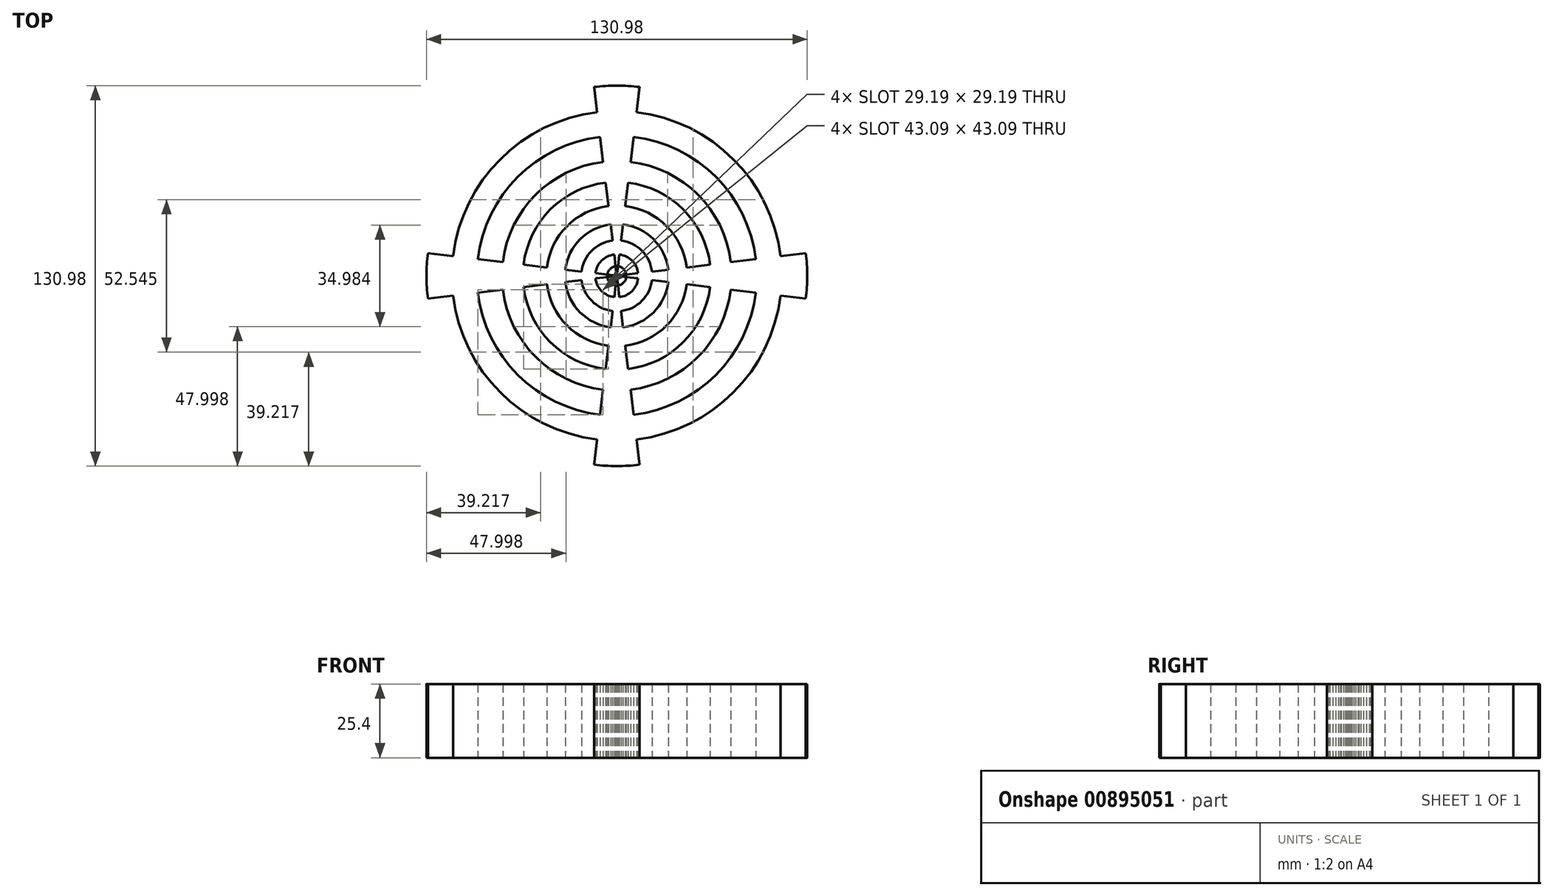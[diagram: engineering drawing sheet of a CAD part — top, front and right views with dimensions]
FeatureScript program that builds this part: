
annotation { "Feature Type Name" : "Feature", "Feature Type Description" : "" }
export const myFeature = defineFeature(function(context is Context, id is Id, definition is map)
    precondition{}
    {
        {
            var Q0;
            Q0=qCreatedBy(makeId("Top.planeOp"),FACE);
            var sketch = newSketch(context, id + "F0", { "sketchPlane" : qUnion([Q0])});
            skCircle(sketch, "E0", {"center": v(0, 0) * mm, "radius": 65.49 * mm});
            skCircle(sketch, "E1", {"center": v(0, 0) * mm, "radius": 56.73 * mm});
            skCircle(sketch, "E2", {"center": v(0, 0) * mm, "radius": 48.16 * mm});
            skCircle(sketch, "E3", {"center": v(0, 0) * mm, "radius": 39.5 * mm});
            skCircle(sketch, "E4", {"center": v(0, 0) * mm, "radius": 32.32 * mm});
            skCircle(sketch, "E5", {"center": v(0, 0) * mm, "radius": 24.2 * mm});
            skCircle(sketch, "E6", {"center": v(0, 0) * mm, "radius": 17.83 * mm});
            skCircle(sketch, "E7", {"center": v(0, 0) * mm, "radius": 12.2 * mm});
            skCircle(sketch, "E8", {"center": v(0, 0) * mm, "radius": 7.4 * mm});
            skCircle(sketch, "E9", {"center": v(0, 0) * mm, "radius": 3.3 * mm});
            skLineSegment(sketch, "E10", {"start": v(0, 0) * mm, "end": v(-7.84, 65.02) * mm});
            skLineSegment(sketch, "E11.MirrorCS", {"start": v(0, 0) * mm, "end": v(7.84, 65.02) * mm});
            skLineSegment(sketch, "E12.MirrorCS", {"start": v(0, 0) * mm, "end": v(-7.84, -65.02) * mm});
            skLineSegment(sketch, "E13.MirrorCS", {"start": v(0, 0) * mm, "end": v(7.84, -65.02) * mm});
            skLineSegment(sketch, "E14", {"start": v(0, 0) * mm, "end": v(65.02, 7.84) * mm});
            skLineSegment(sketch, "E15", {"start": v(0, 0) * mm, "end": v(65.02, -7.84) * mm});
            skLineSegment(sketch, "E16.MirrorCS", {"start": v(0, 0) * mm, "end": v(-65.02, 7.84) * mm});
            skLineSegment(sketch, "E17.MirrorCS", {"start": v(0, 0) * mm, "end": v(-65.02, -7.84) * mm});
            skSolve(sketch);
        }
        {
            var Q0;
            {var subQ0=sQuery(id+"F0.wireOp",EDGE,"E13.MirrorCS");var subQ1=sQuery(id+"F0.wireOp",EDGE,"E9");var subQ2=makeQuery(id+"F0.imprint","INTERSECT",VERTEX,{"derivedFrom":[subQ1,subQ0]});Q0=makeQuery(id+"F0.imprint","IMPRINT",FACE,{"disambiguationData":[TD([[makeQuery(id+"F0.imprint","IMPRINT",EDGE,{"disambiguationData":[TD([[subQ2,-1.0]])],"derivedFrom":subQ1}),1.0]])]});}
            var Q1;
            {var subQ0=sQuery(id+"F0.wireOp",EDGE,"E11.MirrorCS");var subQ1=sQuery(id+"F0.wireOp",EDGE,"E9");var subQ2=makeQuery(id+"F0.imprint","INTERSECT",VERTEX,{"derivedFrom":[subQ1,subQ0]});Q1=makeQuery(id+"F0.imprint","IMPRINT",FACE,{"disambiguationData":[TD([[makeQuery(id+"F0.imprint","IMPRINT",EDGE,{"disambiguationData":[TD([[subQ2,1.0]])],"derivedFrom":subQ1}),1.0]])]});}
            var Q2;
            {var subQ0=sQuery(id+"F0.wireOp",EDGE,"E10");var subQ1=sQuery(id+"F0.wireOp",EDGE,"E9");var subQ2=makeQuery(id+"F0.imprint","INTERSECT",VERTEX,{"derivedFrom":[subQ1,subQ0]});Q2=makeQuery(id+"F0.imprint","IMPRINT",FACE,{"disambiguationData":[TD([[makeQuery(id+"F0.imprint","IMPRINT",EDGE,{"disambiguationData":[TD([[subQ2,-1.0]])],"derivedFrom":subQ1}),1.0]])]});}
            var Q3;
            {var subQ0=sQuery(id+"F0.wireOp",EDGE,"E17.MirrorCS");var subQ1=sQuery(id+"F0.wireOp",EDGE,"E9");var subQ2=makeQuery(id+"F0.imprint","INTERSECT",VERTEX,{"derivedFrom":[subQ1,subQ0]});Q3=makeQuery(id+"F0.imprint","IMPRINT",FACE,{"disambiguationData":[TD([[makeQuery(id+"F0.imprint","IMPRINT",EDGE,{"disambiguationData":[TD([[subQ2,-1.0]])],"derivedFrom":subQ1}),1.0]])]});}
            var Q4;
            {var subQ0=sQuery(id+"F0.wireOp",EDGE,"E10");var subQ1=sQuery(id+"F0.wireOp",EDGE,"E8");var subQ2=makeQuery(id+"F0.imprint","INTERSECT",VERTEX,{"derivedFrom":[subQ1,subQ0]});Q4=makeQuery(id+"F0.imprint","IMPRINT",FACE,{"disambiguationData":[TD([[makeQuery(id+"F0.imprint","IMPRINT",EDGE,{"disambiguationData":[TD([[subQ2,-1.0]])],"derivedFrom":subQ1}),-1.0]])]});}
            var Q5;
            {var subQ0=sQuery(id+"F0.wireOp",EDGE,"E10");var subQ1=sQuery(id+"F0.wireOp",EDGE,"E5");var subQ2=makeQuery(id+"F0.imprint","INTERSECT",VERTEX,{"derivedFrom":[subQ1,subQ0]});Q5=makeQuery(id+"F0.imprint","IMPRINT",FACE,{"disambiguationData":[TD([[makeQuery(id+"F0.imprint","IMPRINT",EDGE,{"disambiguationData":[TD([[subQ2,-1.0]])],"derivedFrom":subQ1}),1.0]])]});}
            var Q6;
            {var subQ0=sQuery(id+"F0.wireOp",EDGE,"E10");var subQ1=sQuery(id+"F0.wireOp",EDGE,"E3");var subQ2=makeQuery(id+"F0.imprint","INTERSECT",VERTEX,{"derivedFrom":[subQ1,subQ0]});Q6=makeQuery(id+"F0.imprint","IMPRINT",FACE,{"disambiguationData":[TD([[makeQuery(id+"F0.imprint","IMPRINT",EDGE,{"disambiguationData":[TD([[subQ2,-1.0]])],"derivedFrom":subQ1}),1.0]])]});}
            var Q7;
            {var subQ0=sQuery(id+"F0.wireOp",EDGE,"E10");var subQ1=sQuery(id+"F0.wireOp",EDGE,"E1");var subQ2=makeQuery(id+"F0.imprint","INTERSECT",VERTEX,{"derivedFrom":[subQ1,subQ0]});Q7=makeQuery(id+"F0.imprint","IMPRINT",FACE,{"disambiguationData":[TD([[makeQuery(id+"F0.imprint","IMPRINT",EDGE,{"disambiguationData":[TD([[subQ2,-1.0]])],"derivedFrom":subQ1}),1.0]])]});}
            var Q8;
            {var subQ0=sQuery(id+"F0.wireOp",EDGE,"E11.MirrorCS");var subQ1=sQuery(id+"F0.wireOp",EDGE,"E1");var subQ2=makeQuery(id+"F0.imprint","INTERSECT",VERTEX,{"derivedFrom":[subQ1,subQ0]});Q8=makeQuery(id+"F0.imprint","IMPRINT",FACE,{"disambiguationData":[TD([[makeQuery(id+"F0.imprint","IMPRINT",EDGE,{"disambiguationData":[TD([[subQ2,1.0]])],"derivedFrom":subQ1}),1.0]])]});}
            var Q9;
            {var subQ0=sQuery(id+"F0.wireOp",EDGE,"E13.MirrorCS");var subQ1=sQuery(id+"F0.wireOp",EDGE,"E1");var subQ2=makeQuery(id+"F0.imprint","INTERSECT",VERTEX,{"derivedFrom":[subQ1,subQ0]});Q9=makeQuery(id+"F0.imprint","IMPRINT",FACE,{"disambiguationData":[TD([[makeQuery(id+"F0.imprint","IMPRINT",EDGE,{"disambiguationData":[TD([[subQ2,-1.0]])],"derivedFrom":subQ1}),1.0]])]});}
            var Q10;
            {var subQ0=sQuery(id+"F0.wireOp",EDGE,"E14");var subQ1=sQuery(id+"F0.wireOp",EDGE,"E2");var subQ2=makeQuery(id+"F0.imprint","INTERSECT",VERTEX,{"derivedFrom":[subQ1,subQ0]});Q10=makeQuery(id+"F0.imprint","IMPRINT",FACE,{"disambiguationData":[TD([[makeQuery(id+"F0.imprint","IMPRINT",EDGE,{"disambiguationData":[TD([[subQ2,1.0]])],"derivedFrom":subQ1}),1.0]])]});}
            var Q11;
            {var subQ0=sQuery(id+"F0.wireOp",EDGE,"E14");var subQ1=sQuery(id+"F0.wireOp",EDGE,"E0");var subQ2=makeQuery(id+"F0.imprint","INTERSECT",VERTEX,{"derivedFrom":[subQ1,subQ0]});Q11=makeQuery(id+"F0.imprint","IMPRINT",FACE,{"disambiguationData":[TD([[makeQuery(id+"F0.imprint","IMPRINT",EDGE,{"disambiguationData":[TD([[subQ2,1.0]])],"derivedFrom":subQ1}),1.0]])]});}
            var Q12;
            {var subQ0=sQuery(id+"F0.wireOp",EDGE,"E14");var subQ1=sQuery(id+"F0.wireOp",EDGE,"E1");var subQ2=makeQuery(id+"F0.imprint","INTERSECT",VERTEX,{"derivedFrom":[subQ1,subQ0]});Q12=makeQuery(id+"F0.imprint","IMPRINT",FACE,{"disambiguationData":[TD([[makeQuery(id+"F0.imprint","IMPRINT",EDGE,{"disambiguationData":[TD([[subQ2,1.0]])],"derivedFrom":subQ1}),1.0]])]});}
            var Q13;
            {var subQ0=sQuery(id+"F0.wireOp",EDGE,"E14");var subQ1=sQuery(id+"F0.wireOp",EDGE,"E3");var subQ2=makeQuery(id+"F0.imprint","INTERSECT",VERTEX,{"derivedFrom":[subQ1,subQ0]});Q13=makeQuery(id+"F0.imprint","IMPRINT",FACE,{"disambiguationData":[TD([[makeQuery(id+"F0.imprint","IMPRINT",EDGE,{"disambiguationData":[TD([[subQ2,1.0]])],"derivedFrom":subQ1}),1.0]])]});}
            var Q14;
            {var subQ0=sQuery(id+"F0.wireOp",EDGE,"E14");var subQ1=sQuery(id+"F0.wireOp",EDGE,"E4");var subQ2=makeQuery(id+"F0.imprint","INTERSECT",VERTEX,{"derivedFrom":[subQ1,subQ0]});Q14=makeQuery(id+"F0.imprint","IMPRINT",FACE,{"disambiguationData":[TD([[makeQuery(id+"F0.imprint","IMPRINT",EDGE,{"disambiguationData":[TD([[subQ2,1.0]])],"derivedFrom":subQ1}),1.0]])]});}
            var Q15;
            {var subQ0=sQuery(id+"F0.wireOp",EDGE,"E14");var subQ1=sQuery(id+"F0.wireOp",EDGE,"E5");var subQ2=makeQuery(id+"F0.imprint","INTERSECT",VERTEX,{"derivedFrom":[subQ1,subQ0]});Q15=makeQuery(id+"F0.imprint","IMPRINT",FACE,{"disambiguationData":[TD([[makeQuery(id+"F0.imprint","IMPRINT",EDGE,{"disambiguationData":[TD([[subQ2,1.0]])],"derivedFrom":subQ1}),1.0]])]});}
            var Q16;
            {var subQ0=sQuery(id+"F0.wireOp",EDGE,"E14");var subQ1=sQuery(id+"F0.wireOp",EDGE,"E6");var subQ2=makeQuery(id+"F0.imprint","INTERSECT",VERTEX,{"derivedFrom":[subQ1,subQ0]});Q16=makeQuery(id+"F0.imprint","IMPRINT",FACE,{"disambiguationData":[TD([[makeQuery(id+"F0.imprint","IMPRINT",EDGE,{"disambiguationData":[TD([[subQ2,1.0]])],"derivedFrom":subQ1}),1.0]])]});}
            var Q17;
            {var subQ0=sQuery(id+"F0.wireOp",EDGE,"E14");var subQ1=sQuery(id+"F0.wireOp",EDGE,"E8");var subQ2=makeQuery(id+"F0.imprint","INTERSECT",VERTEX,{"derivedFrom":[subQ1,subQ0]});Q17=makeQuery(id+"F0.imprint","IMPRINT",FACE,{"disambiguationData":[TD([[makeQuery(id+"F0.imprint","IMPRINT",EDGE,{"disambiguationData":[TD([[subQ2,1.0]])],"derivedFrom":subQ1}),-1.0]])]});}
            var Q18;
            {var subQ0=sQuery(id+"F0.wireOp",EDGE,"E14");var subQ1=sQuery(id+"F0.wireOp",EDGE,"E8");var subQ2=makeQuery(id+"F0.imprint","INTERSECT",VERTEX,{"derivedFrom":[subQ1,subQ0]});Q18=makeQuery(id+"F0.imprint","IMPRINT",FACE,{"disambiguationData":[TD([[makeQuery(id+"F0.imprint","IMPRINT",EDGE,{"disambiguationData":[TD([[subQ2,1.0]])],"derivedFrom":subQ1}),1.0]])]});}
            var Q19;
            {var subQ0=sQuery(id+"F0.wireOp",EDGE,"E17.MirrorCS");var subQ1=sQuery(id+"F0.wireOp",EDGE,"E8");var subQ2=makeQuery(id+"F0.imprint","INTERSECT",VERTEX,{"derivedFrom":[subQ1,subQ0]});Q19=makeQuery(id+"F0.imprint","IMPRINT",FACE,{"disambiguationData":[TD([[makeQuery(id+"F0.imprint","IMPRINT",EDGE,{"disambiguationData":[TD([[subQ2,-1.0]])],"derivedFrom":subQ1}),-1.0]])]});}
            var Q20;
            {var subQ0=sQuery(id+"F0.wireOp",EDGE,"E13.MirrorCS");var subQ1=sQuery(id+"F0.wireOp",EDGE,"E8");var subQ2=makeQuery(id+"F0.imprint","INTERSECT",VERTEX,{"derivedFrom":[subQ1,subQ0]});Q20=makeQuery(id+"F0.imprint","IMPRINT",FACE,{"disambiguationData":[TD([[makeQuery(id+"F0.imprint","IMPRINT",EDGE,{"disambiguationData":[TD([[subQ2,-1.0]])],"derivedFrom":subQ1}),-1.0]])]});}
            var Q21;
            {var subQ0=sQuery(id+"F0.wireOp",EDGE,"E11.MirrorCS");var subQ1=sQuery(id+"F0.wireOp",EDGE,"E8");var subQ2=makeQuery(id+"F0.imprint","INTERSECT",VERTEX,{"derivedFrom":[subQ1,subQ0]});Q21=makeQuery(id+"F0.imprint","IMPRINT",FACE,{"disambiguationData":[TD([[makeQuery(id+"F0.imprint","IMPRINT",EDGE,{"disambiguationData":[TD([[subQ2,1.0]])],"derivedFrom":subQ1}),-1.0]])]});}
            var Q22;
            {var subQ0=sQuery(id+"F0.wireOp",EDGE,"E11.MirrorCS");var subQ1=sQuery(id+"F0.wireOp",EDGE,"E8");var subQ2=makeQuery(id+"F0.imprint","INTERSECT",VERTEX,{"derivedFrom":[subQ1,subQ0]});Q22=makeQuery(id+"F0.imprint","IMPRINT",FACE,{"disambiguationData":[TD([[makeQuery(id+"F0.imprint","IMPRINT",EDGE,{"disambiguationData":[TD([[subQ2,-1.0]])],"derivedFrom":subQ1}),-1.0]])]});}
            var Q23;
            {var subQ0=sQuery(id+"F0.wireOp",EDGE,"E16.MirrorCS");var subQ1=sQuery(id+"F0.wireOp",EDGE,"E8");var subQ2=makeQuery(id+"F0.imprint","INTERSECT",VERTEX,{"derivedFrom":[subQ1,subQ0]});Q23=makeQuery(id+"F0.imprint","IMPRINT",FACE,{"disambiguationData":[TD([[makeQuery(id+"F0.imprint","IMPRINT",EDGE,{"disambiguationData":[TD([[subQ2,-1.0]])],"derivedFrom":subQ1}),-1.0]])]});}
            var Q24;
            {var subQ0=sQuery(id+"F0.wireOp",EDGE,"E12.MirrorCS");var subQ1=sQuery(id+"F0.wireOp",EDGE,"E8");var subQ2=makeQuery(id+"F0.imprint","INTERSECT",VERTEX,{"derivedFrom":[subQ1,subQ0]});Q24=makeQuery(id+"F0.imprint","IMPRINT",FACE,{"disambiguationData":[TD([[makeQuery(id+"F0.imprint","IMPRINT",EDGE,{"disambiguationData":[TD([[subQ2,-1.0]])],"derivedFrom":subQ1}),-1.0]])]});}
            var Q25;
            {var subQ0=sQuery(id+"F0.wireOp",EDGE,"E13.MirrorCS");var subQ1=sQuery(id+"F0.wireOp",EDGE,"E5");var subQ2=makeQuery(id+"F0.imprint","INTERSECT",VERTEX,{"derivedFrom":[subQ1,subQ0]});Q25=makeQuery(id+"F0.imprint","IMPRINT",FACE,{"disambiguationData":[TD([[makeQuery(id+"F0.imprint","IMPRINT",EDGE,{"disambiguationData":[TD([[subQ2,-1.0]])],"derivedFrom":subQ1}),1.0]])]});}
            var Q26;
            {var subQ0=sQuery(id+"F0.wireOp",EDGE,"E11.MirrorCS");var subQ1=sQuery(id+"F0.wireOp",EDGE,"E5");var subQ2=makeQuery(id+"F0.imprint","INTERSECT",VERTEX,{"derivedFrom":[subQ1,subQ0]});Q26=makeQuery(id+"F0.imprint","IMPRINT",FACE,{"disambiguationData":[TD([[makeQuery(id+"F0.imprint","IMPRINT",EDGE,{"disambiguationData":[TD([[subQ2,1.0]])],"derivedFrom":subQ1}),1.0]])]});}
            var Q27;
            {var subQ0=sQuery(id+"F0.wireOp",EDGE,"E11.MirrorCS");var subQ1=sQuery(id+"F0.wireOp",EDGE,"E5");var subQ2=makeQuery(id+"F0.imprint","INTERSECT",VERTEX,{"derivedFrom":[subQ1,subQ0]});Q27=makeQuery(id+"F0.imprint","IMPRINT",FACE,{"disambiguationData":[TD([[makeQuery(id+"F0.imprint","IMPRINT",EDGE,{"disambiguationData":[TD([[subQ2,-1.0]])],"derivedFrom":subQ1}),1.0]])]});}
            var Q28;
            {var subQ0=sQuery(id+"F0.wireOp",EDGE,"E16.MirrorCS");var subQ1=sQuery(id+"F0.wireOp",EDGE,"E5");var subQ2=makeQuery(id+"F0.imprint","INTERSECT",VERTEX,{"derivedFrom":[subQ1,subQ0]});Q28=makeQuery(id+"F0.imprint","IMPRINT",FACE,{"disambiguationData":[TD([[makeQuery(id+"F0.imprint","IMPRINT",EDGE,{"disambiguationData":[TD([[subQ2,-1.0]])],"derivedFrom":subQ1}),1.0]])]});}
            var Q29;
            {var subQ0=sQuery(id+"F0.wireOp",EDGE,"E17.MirrorCS");var subQ1=sQuery(id+"F0.wireOp",EDGE,"E5");var subQ2=makeQuery(id+"F0.imprint","INTERSECT",VERTEX,{"derivedFrom":[subQ1,subQ0]});Q29=makeQuery(id+"F0.imprint","IMPRINT",FACE,{"disambiguationData":[TD([[makeQuery(id+"F0.imprint","IMPRINT",EDGE,{"disambiguationData":[TD([[subQ2,-1.0]])],"derivedFrom":subQ1}),1.0]])]});}
            var Q30;
            {var subQ0=sQuery(id+"F0.wireOp",EDGE,"E16.MirrorCS");var subQ1=sQuery(id+"F0.wireOp",EDGE,"E3");var subQ2=makeQuery(id+"F0.imprint","INTERSECT",VERTEX,{"derivedFrom":[subQ1,subQ0]});Q30=makeQuery(id+"F0.imprint","IMPRINT",FACE,{"disambiguationData":[TD([[makeQuery(id+"F0.imprint","IMPRINT",EDGE,{"disambiguationData":[TD([[subQ2,-1.0]])],"derivedFrom":subQ1}),1.0]])]});}
            var Q31;
            {var subQ0=sQuery(id+"F0.wireOp",EDGE,"E17.MirrorCS");var subQ1=sQuery(id+"F0.wireOp",EDGE,"E3");var subQ2=makeQuery(id+"F0.imprint","INTERSECT",VERTEX,{"derivedFrom":[subQ1,subQ0]});Q31=makeQuery(id+"F0.imprint","IMPRINT",FACE,{"disambiguationData":[TD([[makeQuery(id+"F0.imprint","IMPRINT",EDGE,{"disambiguationData":[TD([[subQ2,-1.0]])],"derivedFrom":subQ1}),1.0]])]});}
            var Q32;
            {var subQ0=sQuery(id+"F0.wireOp",EDGE,"E13.MirrorCS");var subQ1=sQuery(id+"F0.wireOp",EDGE,"E3");var subQ2=makeQuery(id+"F0.imprint","INTERSECT",VERTEX,{"derivedFrom":[subQ1,subQ0]});Q32=makeQuery(id+"F0.imprint","IMPRINT",FACE,{"disambiguationData":[TD([[makeQuery(id+"F0.imprint","IMPRINT",EDGE,{"disambiguationData":[TD([[subQ2,-1.0]])],"derivedFrom":subQ1}),1.0]])]});}
            var Q33;
            {var subQ0=sQuery(id+"F0.wireOp",EDGE,"E12.MirrorCS");var subQ1=sQuery(id+"F0.wireOp",EDGE,"E3");var subQ2=makeQuery(id+"F0.imprint","INTERSECT",VERTEX,{"derivedFrom":[subQ1,subQ0]});Q33=makeQuery(id+"F0.imprint","IMPRINT",FACE,{"disambiguationData":[TD([[makeQuery(id+"F0.imprint","IMPRINT",EDGE,{"disambiguationData":[TD([[subQ2,-1.0]])],"derivedFrom":subQ1}),1.0]])]});}
            var Q34;
            {var subQ0=sQuery(id+"F0.wireOp",EDGE,"E11.MirrorCS");var subQ1=sQuery(id+"F0.wireOp",EDGE,"E3");var subQ2=makeQuery(id+"F0.imprint","INTERSECT",VERTEX,{"derivedFrom":[subQ1,subQ0]});Q34=makeQuery(id+"F0.imprint","IMPRINT",FACE,{"disambiguationData":[TD([[makeQuery(id+"F0.imprint","IMPRINT",EDGE,{"disambiguationData":[TD([[subQ2,1.0]])],"derivedFrom":subQ1}),1.0]])]});}
            var Q35;
            {var subQ0=sQuery(id+"F0.wireOp",EDGE,"E11.MirrorCS");var subQ1=sQuery(id+"F0.wireOp",EDGE,"E1");var subQ2=makeQuery(id+"F0.imprint","INTERSECT",VERTEX,{"derivedFrom":[subQ1,subQ0]});Q35=makeQuery(id+"F0.imprint","IMPRINT",FACE,{"disambiguationData":[TD([[makeQuery(id+"F0.imprint","IMPRINT",EDGE,{"disambiguationData":[TD([[subQ2,-1.0]])],"derivedFrom":subQ1}),1.0]])]});}
            var Q36;
            {var subQ0=sQuery(id+"F0.wireOp",EDGE,"E16.MirrorCS");var subQ1=sQuery(id+"F0.wireOp",EDGE,"E1");var subQ2=makeQuery(id+"F0.imprint","INTERSECT",VERTEX,{"derivedFrom":[subQ1,subQ0]});Q36=makeQuery(id+"F0.imprint","IMPRINT",FACE,{"disambiguationData":[TD([[makeQuery(id+"F0.imprint","IMPRINT",EDGE,{"disambiguationData":[TD([[subQ2,-1.0]])],"derivedFrom":subQ1}),1.0]])]});}
            var Q37;
            {var subQ0=sQuery(id+"F0.wireOp",EDGE,"E17.MirrorCS");var subQ1=sQuery(id+"F0.wireOp",EDGE,"E1");var subQ2=makeQuery(id+"F0.imprint","INTERSECT",VERTEX,{"derivedFrom":[subQ1,subQ0]});Q37=makeQuery(id+"F0.imprint","IMPRINT",FACE,{"disambiguationData":[TD([[makeQuery(id+"F0.imprint","IMPRINT",EDGE,{"disambiguationData":[TD([[subQ2,-1.0]])],"derivedFrom":subQ1}),1.0]])]});}
            var Q38;
            {var subQ0=sQuery(id+"F0.wireOp",EDGE,"E12.MirrorCS");var subQ1=sQuery(id+"F0.wireOp",EDGE,"E1");var subQ2=makeQuery(id+"F0.imprint","INTERSECT",VERTEX,{"derivedFrom":[subQ1,subQ0]});Q38=makeQuery(id+"F0.imprint","IMPRINT",FACE,{"disambiguationData":[TD([[makeQuery(id+"F0.imprint","IMPRINT",EDGE,{"disambiguationData":[TD([[subQ2,-1.0]])],"derivedFrom":subQ1}),1.0]])]});}
            var Q39;
            {var subQ0=sQuery(id+"F0.wireOp",EDGE,"E12.MirrorCS");var subQ1=sQuery(id+"F0.wireOp",EDGE,"E2");var subQ2=makeQuery(id+"F0.imprint","INTERSECT",VERTEX,{"derivedFrom":[subQ1,subQ0]});Q39=makeQuery(id+"F0.imprint","IMPRINT",FACE,{"disambiguationData":[TD([[makeQuery(id+"F0.imprint","IMPRINT",EDGE,{"disambiguationData":[TD([[subQ2,-1.0]])],"derivedFrom":subQ1}),1.0]])]});}
            var Q40;
            {var subQ0=sQuery(id+"F0.wireOp",EDGE,"E12.MirrorCS");var subQ1=sQuery(id+"F0.wireOp",EDGE,"E0");var subQ2=makeQuery(id+"F0.imprint","INTERSECT",VERTEX,{"derivedFrom":[subQ1,subQ0]});Q40=makeQuery(id+"F0.imprint","IMPRINT",FACE,{"disambiguationData":[TD([[makeQuery(id+"F0.imprint","IMPRINT",EDGE,{"disambiguationData":[TD([[subQ2,-1.0]])],"derivedFrom":subQ1}),1.0]])]});}
            var Q41;
            {var subQ0=sQuery(id+"F0.wireOp",EDGE,"E12.MirrorCS");var subQ1=sQuery(id+"F0.wireOp",EDGE,"E4");var subQ2=makeQuery(id+"F0.imprint","INTERSECT",VERTEX,{"derivedFrom":[subQ1,subQ0]});Q41=makeQuery(id+"F0.imprint","IMPRINT",FACE,{"disambiguationData":[TD([[makeQuery(id+"F0.imprint","IMPRINT",EDGE,{"disambiguationData":[TD([[subQ2,-1.0]])],"derivedFrom":subQ1}),1.0]])]});}
            var Q42;
            {var subQ0=sQuery(id+"F0.wireOp",EDGE,"E12.MirrorCS");var subQ1=sQuery(id+"F0.wireOp",EDGE,"E6");var subQ2=makeQuery(id+"F0.imprint","INTERSECT",VERTEX,{"derivedFrom":[subQ1,subQ0]});Q42=makeQuery(id+"F0.imprint","IMPRINT",FACE,{"disambiguationData":[TD([[makeQuery(id+"F0.imprint","IMPRINT",EDGE,{"disambiguationData":[TD([[subQ2,-1.0]])],"derivedFrom":subQ1}),1.0]])]});}
            var Q43;
            {var subQ0=sQuery(id+"F0.wireOp",EDGE,"E12.MirrorCS");var subQ1=sQuery(id+"F0.wireOp",EDGE,"E5");var subQ2=makeQuery(id+"F0.imprint","INTERSECT",VERTEX,{"derivedFrom":[subQ1,subQ0]});Q43=makeQuery(id+"F0.imprint","IMPRINT",FACE,{"disambiguationData":[TD([[makeQuery(id+"F0.imprint","IMPRINT",EDGE,{"disambiguationData":[TD([[subQ2,-1.0]])],"derivedFrom":subQ1}),1.0]])]});}
            var Q44;
            {var subQ0=sQuery(id+"F0.wireOp",EDGE,"E16.MirrorCS");var subQ1=sQuery(id+"F0.wireOp",EDGE,"E6");var subQ2=makeQuery(id+"F0.imprint","INTERSECT",VERTEX,{"derivedFrom":[subQ1,subQ0]});Q44=makeQuery(id+"F0.imprint","IMPRINT",FACE,{"disambiguationData":[TD([[makeQuery(id+"F0.imprint","IMPRINT",EDGE,{"disambiguationData":[TD([[subQ2,-1.0]])],"derivedFrom":subQ1}),1.0]])]});}
            var Q45;
            {var subQ0=sQuery(id+"F0.wireOp",EDGE,"E16.MirrorCS");var subQ1=sQuery(id+"F0.wireOp",EDGE,"E4");var subQ2=makeQuery(id+"F0.imprint","INTERSECT",VERTEX,{"derivedFrom":[subQ1,subQ0]});Q45=makeQuery(id+"F0.imprint","IMPRINT",FACE,{"disambiguationData":[TD([[makeQuery(id+"F0.imprint","IMPRINT",EDGE,{"disambiguationData":[TD([[subQ2,-1.0]])],"derivedFrom":subQ1}),1.0]])]});}
            var Q46;
            {var subQ0=sQuery(id+"F0.wireOp",EDGE,"E16.MirrorCS");var subQ1=sQuery(id+"F0.wireOp",EDGE,"E2");var subQ2=makeQuery(id+"F0.imprint","INTERSECT",VERTEX,{"derivedFrom":[subQ1,subQ0]});Q46=makeQuery(id+"F0.imprint","IMPRINT",FACE,{"disambiguationData":[TD([[makeQuery(id+"F0.imprint","IMPRINT",EDGE,{"disambiguationData":[TD([[subQ2,-1.0]])],"derivedFrom":subQ1}),1.0]])]});}
            var Q47;
            {var subQ0=sQuery(id+"F0.wireOp",EDGE,"E16.MirrorCS");var subQ1=sQuery(id+"F0.wireOp",EDGE,"E0");var subQ2=makeQuery(id+"F0.imprint","INTERSECT",VERTEX,{"derivedFrom":[subQ1,subQ0]});Q47=makeQuery(id+"F0.imprint","IMPRINT",FACE,{"disambiguationData":[TD([[makeQuery(id+"F0.imprint","IMPRINT",EDGE,{"disambiguationData":[TD([[subQ2,-1.0]])],"derivedFrom":subQ1}),1.0]])]});}
            var Q48;
            {var subQ0=sQuery(id+"F0.wireOp",EDGE,"E11.MirrorCS");var subQ1=sQuery(id+"F0.wireOp",EDGE,"E0");var subQ2=makeQuery(id+"F0.imprint","INTERSECT",VERTEX,{"derivedFrom":[subQ1,subQ0]});Q48=makeQuery(id+"F0.imprint","IMPRINT",FACE,{"disambiguationData":[TD([[makeQuery(id+"F0.imprint","IMPRINT",EDGE,{"disambiguationData":[TD([[subQ2,-1.0]])],"derivedFrom":subQ1}),1.0]])]});}
            var Q49;
            {var subQ0=sQuery(id+"F0.wireOp",EDGE,"E11.MirrorCS");var subQ1=sQuery(id+"F0.wireOp",EDGE,"E2");var subQ2=makeQuery(id+"F0.imprint","INTERSECT",VERTEX,{"derivedFrom":[subQ1,subQ0]});Q49=makeQuery(id+"F0.imprint","IMPRINT",FACE,{"disambiguationData":[TD([[makeQuery(id+"F0.imprint","IMPRINT",EDGE,{"disambiguationData":[TD([[subQ2,-1.0]])],"derivedFrom":subQ1}),1.0]])]});}
            var Q50;
            {var subQ0=sQuery(id+"F0.wireOp",EDGE,"E11.MirrorCS");var subQ1=sQuery(id+"F0.wireOp",EDGE,"E4");var subQ2=makeQuery(id+"F0.imprint","INTERSECT",VERTEX,{"derivedFrom":[subQ1,subQ0]});Q50=makeQuery(id+"F0.imprint","IMPRINT",FACE,{"disambiguationData":[TD([[makeQuery(id+"F0.imprint","IMPRINT",EDGE,{"disambiguationData":[TD([[subQ2,-1.0]])],"derivedFrom":subQ1}),1.0]])]});}
            var Q51;
            {var subQ0=sQuery(id+"F0.wireOp",EDGE,"E11.MirrorCS");var subQ1=sQuery(id+"F0.wireOp",EDGE,"E6");var subQ2=makeQuery(id+"F0.imprint","INTERSECT",VERTEX,{"derivedFrom":[subQ1,subQ0]});Q51=makeQuery(id+"F0.imprint","IMPRINT",FACE,{"disambiguationData":[TD([[makeQuery(id+"F0.imprint","IMPRINT",EDGE,{"disambiguationData":[TD([[subQ2,-1.0]])],"derivedFrom":subQ1}),1.0]])]});}
            var Q52;
            {var subQ0=sQuery(id+"F0.wireOp",EDGE,"E11.MirrorCS");var subQ1=sQuery(id+"F0.wireOp",EDGE,"E3");var subQ2=makeQuery(id+"F0.imprint","INTERSECT",VERTEX,{"derivedFrom":[subQ1,subQ0]});Q52=makeQuery(id+"F0.imprint","IMPRINT",FACE,{"disambiguationData":[TD([[makeQuery(id+"F0.imprint","IMPRINT",EDGE,{"disambiguationData":[TD([[subQ2,-1.0]])],"derivedFrom":subQ1}),1.0]])]});}
            var Q53;
            {var subQ0=sQuery(id+"F0.wireOp",EDGE,"E12.MirrorCS");var subQ1=sQuery(id+"F0.wireOp",EDGE,"E8");var subQ2=makeQuery(id+"F0.imprint","INTERSECT",VERTEX,{"derivedFrom":[subQ1,subQ0]});Q53=makeQuery(id+"F0.imprint","IMPRINT",FACE,{"disambiguationData":[TD([[makeQuery(id+"F0.imprint","IMPRINT",EDGE,{"disambiguationData":[TD([[subQ2,-1.0]])],"derivedFrom":subQ1}),1.0]])]});}
            var Q54;
            {var subQ0=sQuery(id+"F0.wireOp",EDGE,"E11.MirrorCS");var subQ1=sQuery(id+"F0.wireOp",EDGE,"E8");var subQ2=makeQuery(id+"F0.imprint","INTERSECT",VERTEX,{"derivedFrom":[subQ1,subQ0]});Q54=makeQuery(id+"F0.imprint","IMPRINT",FACE,{"disambiguationData":[TD([[makeQuery(id+"F0.imprint","IMPRINT",EDGE,{"disambiguationData":[TD([[subQ2,-1.0]])],"derivedFrom":subQ1}),1.0]])]});}
            var Q55;
            {var subQ0=sQuery(id+"F0.wireOp",EDGE,"E16.MirrorCS");var subQ1=sQuery(id+"F0.wireOp",EDGE,"E8");var subQ2=makeQuery(id+"F0.imprint","INTERSECT",VERTEX,{"derivedFrom":[subQ1,subQ0]});Q55=makeQuery(id+"F0.imprint","IMPRINT",FACE,{"disambiguationData":[TD([[makeQuery(id+"F0.imprint","IMPRINT",EDGE,{"disambiguationData":[TD([[subQ2,-1.0]])],"derivedFrom":subQ1}),1.0]])]});}
            extrude(context, id + "F1", {"entities" : qUnion([Q0, Q1, Q2, Q3, Q4, Q5, Q6, Q7, Q8, Q9, Q10, Q11, Q12, Q13, Q14, Q15, Q16, Q17, Q18, Q19, Q20, Q21, Q22, Q23, Q24, Q25, Q26, Q27, Q28, Q29, Q30, Q31, Q32, Q33, Q34, Q35, Q36, Q37, Q38, Q39, Q40, Q41, Q42, Q43, Q44, Q45, Q46, Q47, Q48, Q49, Q50, Q51, Q52, Q53, Q54, Q55]), "depth" : 25.4 * mm, "offsetDistance" : 25.4 * mm});
        }
    });
